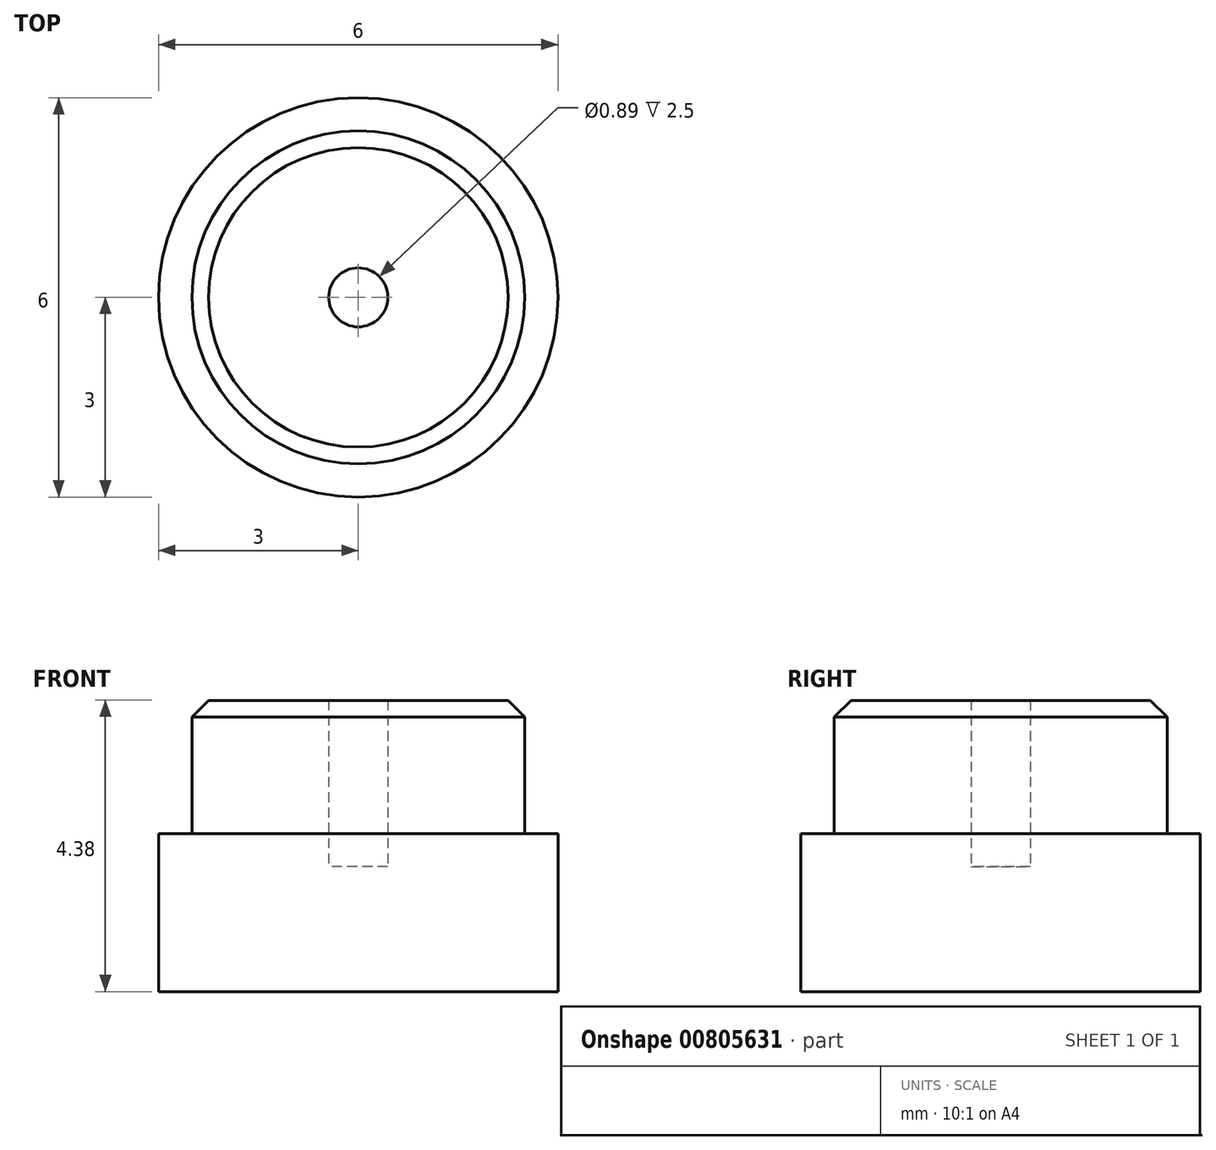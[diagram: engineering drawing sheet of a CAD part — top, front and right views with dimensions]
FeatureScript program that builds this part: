
annotation { "Feature Type Name" : "Feature", "Feature Type Description" : "" }
export const myFeature = defineFeature(function(context is Context, id is Id, definition is map)
    precondition{}
    {
        {
            var Q0;
            Q0=qCreatedBy(makeId("Top.planeOp"),FACE);
            var sketch = newSketch(context, id + "F0", { "sketchPlane" : qUnion([Q0])});
            skCircle(sketch, "E0", {"center": v(0, 0) * mm, "radius": 0.44 * mm});
            skCircle(sketch, "E1", {"center": v(0, 0) * mm, "radius": 3 * mm});
            skCircle(sketch, "E2", {"center": v(0, 0) * mm, "radius": 2.5 * mm});
            skSolve(sketch);
        }
        {
            var Q0;
            Q0=makeQuery(id+"F0.imprint","IMPRINT",FACE,{"disambiguationData":[TD([[makeQuery(id+"F0.imprint","IMPRINT",EDGE,{"derivedFrom":sQuery(id+"F0.wireOp",EDGE,"E2")}),1.0]])]});
            extrude(context, id + "F1", {"entities" : qUnion([Q0]), "depth" : 3.38 * mm, "offsetDistance" : 25 * mm});
        }
        {
            var Q0;
            Q0=makeQuery(id+"F0.imprint","IMPRINT",FACE,{"disambiguationData":[TD([[makeQuery(id+"F0.imprint","IMPRINT",EDGE,{"derivedFrom":sQuery(id+"F0.wireOp",EDGE,"E1")}),1.0]])]});
            extrude(context, id + "F2", {"entities" : qUnion([Q0]), "operationType" : NewBodyOperationType.ADD, "depth" : 1.38 * mm, "offsetDistance" : 25 * mm});
        }
        {
            var Q0;
            Q0=makeQuery(id+"F0.imprint","IMPRINT",FACE,{"disambiguationData":[TD([[makeQuery(id+"F0.imprint","IMPRINT",EDGE,{"derivedFrom":sQuery(id+"F0.wireOp",EDGE,"E0")}),1.0]])]});
            extrude(context, id + "F3", {"entities" : qUnion([Q0]), "operationType" : NewBodyOperationType.ADD, "depth" : .875 * mm, "offsetDistance" : 25 * mm});
        }
        {
            var Q0;
            Q0=makeQuery(id+"F1.opExtrude","CAP_EDGE",EDGE,{"disambiguationData":[OSD([sQuery(id+"F0.wireOp",EDGE,"E2")])],"isStart":false});
            chamfer(context, id + "F4", {"entities" : qUnion([Q0]), "width" : .25 * mm, "tangentPropagation" : true});
        }
        {
            var Q0;
            Q0=makeQuery(id+"F0.imprint","IMPRINT",FACE,{"disambiguationData":[TD([[makeQuery(id+"F0.imprint","IMPRINT",EDGE,{"derivedFrom":sQuery(id+"F0.wireOp",EDGE,"E0")}),1.0]])]});
            var Q1;
            Q1=makeQuery(id+"F0.imprint","IMPRINT",FACE,{"disambiguationData":[TD([[makeQuery(id+"F0.imprint","IMPRINT",EDGE,{"derivedFrom":sQuery(id+"F0.wireOp",EDGE,"E2")}),1.0]])]});
            var Q2;
            Q2=makeQuery(id+"F0.imprint","IMPRINT",FACE,{"disambiguationData":[TD([[makeQuery(id+"F0.imprint","IMPRINT",EDGE,{"derivedFrom":sQuery(id+"F0.wireOp",EDGE,"E1")}),1.0]])]});
            extrude(context, id + "F5", {"entities" : qUnion([Q0, Q1, Q2]), "operationType" : NewBodyOperationType.ADD, "oppositeDirection" : true, "depth" : 1 * mm, "offsetDistance" : 25 * mm});
        }
        {
            var Q0;
            Q0=qCreatedBy(makeId("Right.planeOp"),FACE);
            var sketch = newSketch(context, id + "F6", { "sketchPlane" : qUnion([Q0])});
            skLineSegment(sketch, "E3", {"start": v(-6.7, 0) * mm, "end": v(-3.12, 0.96) * mm});
            skLineSegment(sketch, "E4", {"start": v(-3.12, 0.96) * mm, "end": v(-6.7, 0.96) * mm});
            skLineSegment(sketch, "E5", {"start": v(-6.7, 0.96) * mm, "end": v(-6.7, 0) * mm});
            skLineSegment(sketch, "E6", {"start": v(0, -2.7) * mm, "end": v(0, 4.57) * mm, "construction": true});
            skSolve(sketch);
        }
        {
            var Q0;
            Q0=makeQuery(id+"F6.imprint","IMPRINT",FACE,{"disambiguationData":[TD([[makeQuery(id+"F6.imprint","IMPRINT",EDGE,{"derivedFrom":sQuery(id+"F6.wireOp",EDGE,"E3")}),1.0]])]});
            var Q1;
            Q1=sQuery(id+"F6.wireOp",EDGE,"E6");
            revolve(context, id + "F7", {"operationType" : NewBodyOperationType.REMOVE, "surfaceOperationType" : NewSurfaceOperationType.NEW, "entities" : qUnion([Q0]), "axis" : qUnion([Q1]), "revolveType" : RevolveType.FULL, "oppositeDirection" : true});
        }
    });
